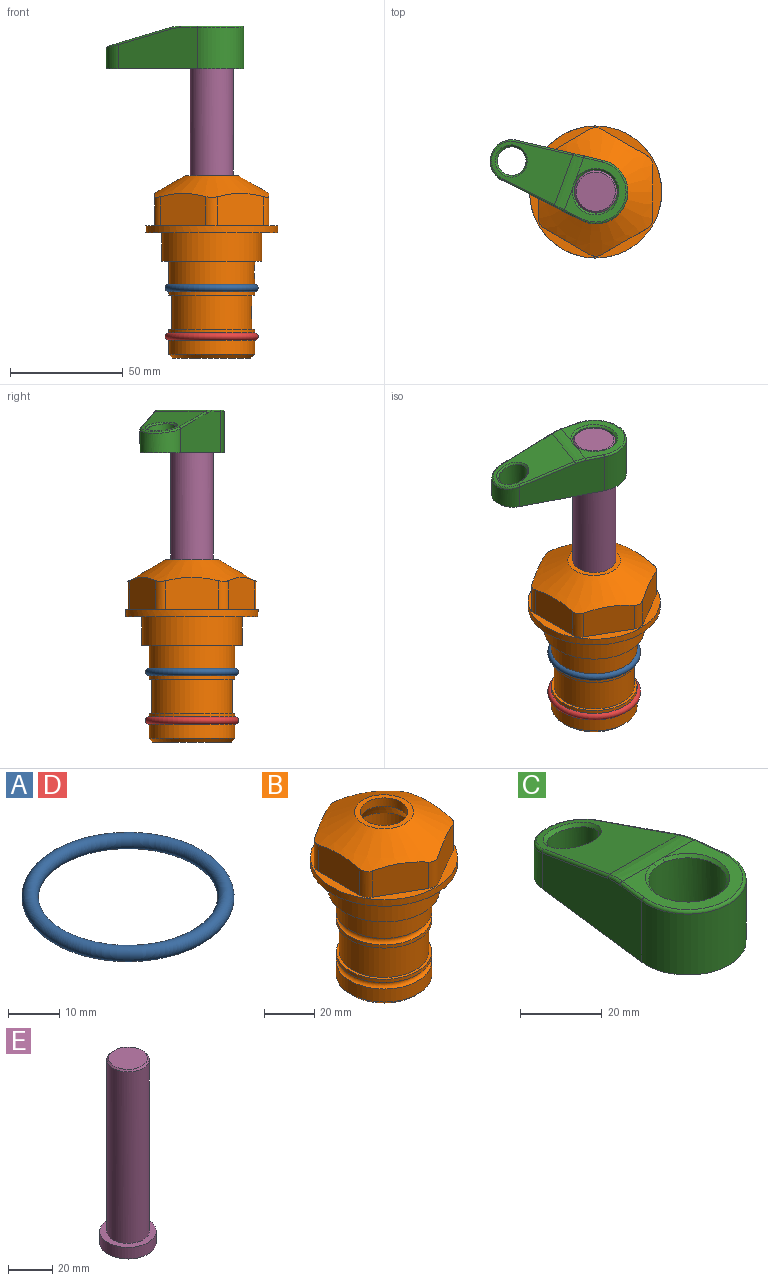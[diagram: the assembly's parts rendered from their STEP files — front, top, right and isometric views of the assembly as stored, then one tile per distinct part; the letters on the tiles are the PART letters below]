
ASSEMBLY  parts=5 mates=4
PART A: 1 faces, bbox 44.7x44.7x3.2 mm
  f0: torus R=19.05mm, axis (0,0,1), area 1193.9mm2
PART B: 36 faces, bbox 58.7x58.7x81 mm
  f0: cylinder r=17.78mm len=35.56mm, axis (0,0,1), area 1670.8mm2, adj f23,f24,f31
  f1: cylinder r=19.05mm len=38.1mm, axis (0,0,1), area 1191.9mm2, adj f26,f27,f30
  f2: plane 58.66x58.66mm, normal (0,0,-1), area 1150.6mm2, adj f3,f28
  f3: cylinder r=29.33mm len=58.66mm, axis (0,0,-1), area 585.1mm2, adj f2,f4
  f4: plane 58.66x58.66mm, normal (0,0,1), area 475.9mm2, adj f3,f5,f6,f7,f8,f9,f10,f11
  f5: plane 20.32x14.34mm, normal (-0.5,0.87,0), area 324.4mm2, adj f4,f15,f16,f17
  f6: plane 20.32x14.34mm, normal (0.5,0.87,0), area 324.4mm2, adj f4,f14,f15,f17
  f7: plane 23.48x14.34mm, normal (1,0,0), area 324.4mm2, adj f4,f13,f14,f17
  f8: plane 20.32x14.34mm, normal (0.5,-0.87,0), area 324.4mm2, adj f4,f12,f13,f17
  f9: plane 20.32x14.34mm, normal (-0.5,-0.87,0), area 324.4mm2, adj f4,f11,f12,f17
  f10: plane 23.48x14.34mm, normal (-1,0,0), area 324.4mm2, adj f4,f11,f16,f17
  f11: cylinder r=5.08mm len=12.85mm, axis (0,0,-1), area 67.2mm2, adj f4,f9,f10,f17
  f12: cylinder r=5.08mm len=12.85mm, axis (0,0,-1), area 67.2mm2, adj f4,f8,f9,f17
  f13: cylinder r=5.08mm len=12.85mm, axis (0,0,-1), area 67.2mm2, adj f4,f7,f8,f17
  f14: cylinder r=5.08mm len=12.85mm, axis (0,0,-1), area 67.2mm2, adj f4,f6,f7,f17
  f15: cylinder r=5.08mm len=12.85mm, axis (0,0,-1), area 67.2mm2, adj f4,f5,f6,f17
  f16: cylinder r=5.08mm len=12.85mm, axis (0,0,-1), area 67.2mm2, adj f4,f5,f10,f17
  f17: cone r=11.73mm half-angle=60deg, axis (0,0,-1), area 2071.8mm2, adj f5,f6,f7,f8,f9,f10,f11,f12
  f18: plane 23.46x23.46mm, normal (0,0,1), area 147.4mm2, adj f17,f35
  f19: plane 34.93x34.93mm, normal (0,0,-1), area 958mm2, adj f29
  f20: cylinder r=19.05mm len=38.1mm, axis (0,0,1), area 760.1mm2, adj f21,f29
  f21: torus R=19.05mm, axis (0,0,1), area 565.3mm2, adj f20,f22
  f22: cylinder r=19.05mm len=38.1mm, axis (0,0,1), area 190mm2, adj f21,f23
  f23: plane 38.1x38.1mm, normal (0,0,1), area 146.9mm2, adj f0,f22
  f24: plane 38.1x38.1mm, normal (0,0,-1), area 146.9mm2, adj f0,f25
  f25: cylinder r=19.05mm len=38.1mm, axis (0,0,1), area 190mm2, adj f24,f26
  f26: torus R=19.05mm, axis (0,0,1), area 565.3mm2, adj f1,f25
  f27: plane 44.45x44.45mm, normal (0,0,-1), area 411.7mm2, adj f1,f28
  f28: cylinder r=22.23mm len=44.45mm, axis (0,0,1), area 1773.5mm2, adj f2,f27
  f29: cone r=19.05mm half-angle=45deg, axis (0,0,1), area 257.5mm2, adj f19,f20
  f30: cylinder r=3.17mm len=6.75mm, axis (-1,0,0), area 128mm2, adj f1,f33
  f31: cylinder r=3.17mm len=6.35mm, axis (-1,0,0), area 102.5mm2, adj f0,f33
  f32: plane 25.4x25.4mm, normal (0,0,1), area 506.7mm2, adj f33
  f33: cylinder r=12.7mm len=66.42mm, axis (0,0,-1), area 5236.2mm2, adj f30,f31,f32,f34
  f34: cone r=9.53mm half-angle=30deg, axis (0,0,-1), area 443.4mm2, adj f33,f35
  f35: cylinder r=9.53mm len=19.05mm, axis (0,0,-1), area 240.9mm2, adj f18,f34
PART C: 31 faces, bbox 31.7x65.5x19.8 mm
  f0: plane 39.12x18.26mm, normal (0.99,0.12,0), area 612.2mm2, adj f1,f4,f7,f11,f13,f15
  f1: cylinder r=9.53mm len=18.91mm, axis (0,0,-1), area 296.1mm2, adj f0,f2,f7,f17
  f2: plane 39.12x18.26mm, normal (-0.99,0.12,0), area 612.2mm2, adj f1,f4,f7,f12,f14,f16
  f3: cylinder r=6.35mm len=12.7mm, axis (0,0,-1), area 362.4mm2, adj f7,f18
  f4: cylinder r=14.29mm len=28.58mm, axis (0,0,-1), area 882.2mm2, adj f0,f2,f7,f10
  f5: cylinder r=9.53mm len=19.05mm, axis (0,0,-1), area 1092.6mm2, adj f7,f19,f20
  f6: plane 26.99x23.69mm, normal (0,0,1), area 216.2mm2, adj f9,f10,f11,f12,f19
  f7: plane 63.5x28.58mm, normal (0,0,-1), area 661.8mm2, adj f0,f1,f2,f3,f4,f5,f22,f23
  f8: plane 33.52x23.6mm, normal (0,0.26,0.97), area 486mm2, adj f9,f15,f16,f17,f18
  f9: cylinder r=19.05mm len=24.72mm, axis (1,0,0), area 120.4mm2, adj f6,f8,f13,f14,f20
  f10: torus R=13.49mm, axis (0,0,1), area 59mm2, adj f4,f6,f11,f12
  f11: cylinder r=0.79mm len=8.67mm, axis (0.12,-0.99,0), area 10.8mm2, adj f0,f6,f10,f13
  f12: cylinder r=0.79mm len=8.67mm, axis (0.12,0.99,0), area 10.8mm2, adj f2,f6,f10,f14
  f13: bspline ~4.95x1.42mm, area 6.1mm2, adj f0,f9,f11,f15
  f14: bspline ~4.95x1.42mm, area 6.1mm2, adj f2,f9,f12,f16
  f15: cylinder r=0.79mm len=25.95mm, axis (0.12,-0.96,0.26), area 32.9mm2, adj f0,f8,f13,f17
  f16: cylinder r=0.79mm len=25.95mm, axis (0.12,0.96,-0.26), area 32.9mm2, adj f2,f8,f14,f17
  f17: bspline ~18.91x8.38mm, area 30mm2, adj f1,f8,f15,f16
  f18: bspline ~14.29x14.29mm, area 48.3mm2, adj f3,f8
  f19: cone r=9.53mm half-angle=45deg, axis (0,0,1), area 66.5mm2, adj f5,f6,f20
  f20: bspline ~3.22x0.96mm, area 3.5mm2, adj f5,f9,f19
  f21: plane 2.75x2.72mm, normal (0,0,-1), area 2.9mm2, adj f23,f25,f28
  f22: plane 23.05x15.88mm, normal (-0.99,-0.12,0), area 323.6mm2, adj f7,f25,f26,f27,f28,f29
  f23: plane 23.05x15.88mm, normal (0.99,-0.12,0), area 323.6mm2, adj f7,f21,f25,f27,f28,f30
  f24: cylinder r=9.53mm len=10.69mm, axis (0,0,-1), area 114.7mm2, adj f7,f27,f29,f30
  f25: cylinder r=12.7mm len=20.59mm, axis (0,0,-1), area 381.1mm2, adj f7,f21,f22,f23,f26,f28
  f26: plane 2.75x2.72mm, normal (0,0,-1), area 2.9mm2, adj f22,f25,f28
  f27: plane 19.72x18.37mm, normal (0,-0.26,-0.97), area 291.8mm2, adj f22,f23,f24,f28,f29,f30
  f28: cylinder r=15.88mm len=19.92mm, axis (1,0,0), area 54.8mm2, adj f21,f22,f23,f25,f26,f27
  f29: cylinder r=1.59mm len=11mm, axis (0,0,-1), area 34.7mm2, adj f7,f22,f24,f27
  f30: cylinder r=1.59mm len=11mm, axis (0,0,-1), area 34.7mm2, adj f7,f23,f24,f27
PART D: same geometry as A
PART E: 6 faces, bbox 25.4x25.4x101.6 mm
  f0: plane 17.46x17.46mm, normal (0,0,1), area 239.5mm2, adj f5
  f1: plane 25.4x25.4mm, normal (0,0,-1), area 506.7mm2, adj f2
  f2: cylinder r=12.7mm len=25.4mm, axis (0,0,1), area 506.7mm2, adj f1,f3
  f3: plane 25.4x25.4mm, normal (0,0,1), area 221.7mm2, adj f2,f4
  f4: cylinder r=9.53mm len=94.46mm, axis (0,0,1), area 5653mm2, adj f3,f5
  f5: cone r=8.73mm half-angle=45deg, axis (0,0,-1), area 64.4mm2, adj f0,f4
PLACE A at identity
PLACE B at identity fixed
PLACE C rot(axis=(0,0,1),70deg) t=(0,0,28.35)mm
PLACE D t=(0,0,-21.59)mm
PLACE E rot(axis=(0,0,1),70deg) t=(0,0,27.55)mm
MATE fastened D.f0 <-> B.f0  axis (0,0,1) through (0,0,-46.1)mm
MATE fastened A.f0 <-> B.f0  axis (0,0,1) through (0,0,-24.51)mm
MATE cylindrical E.f2 <-> B.f0  axis (0,0,-1) through (0,0,-10.55)mm
MATE fastened E.f2 <-> C.f4  axis (0,0,1) through (0,0,91.05)mm
